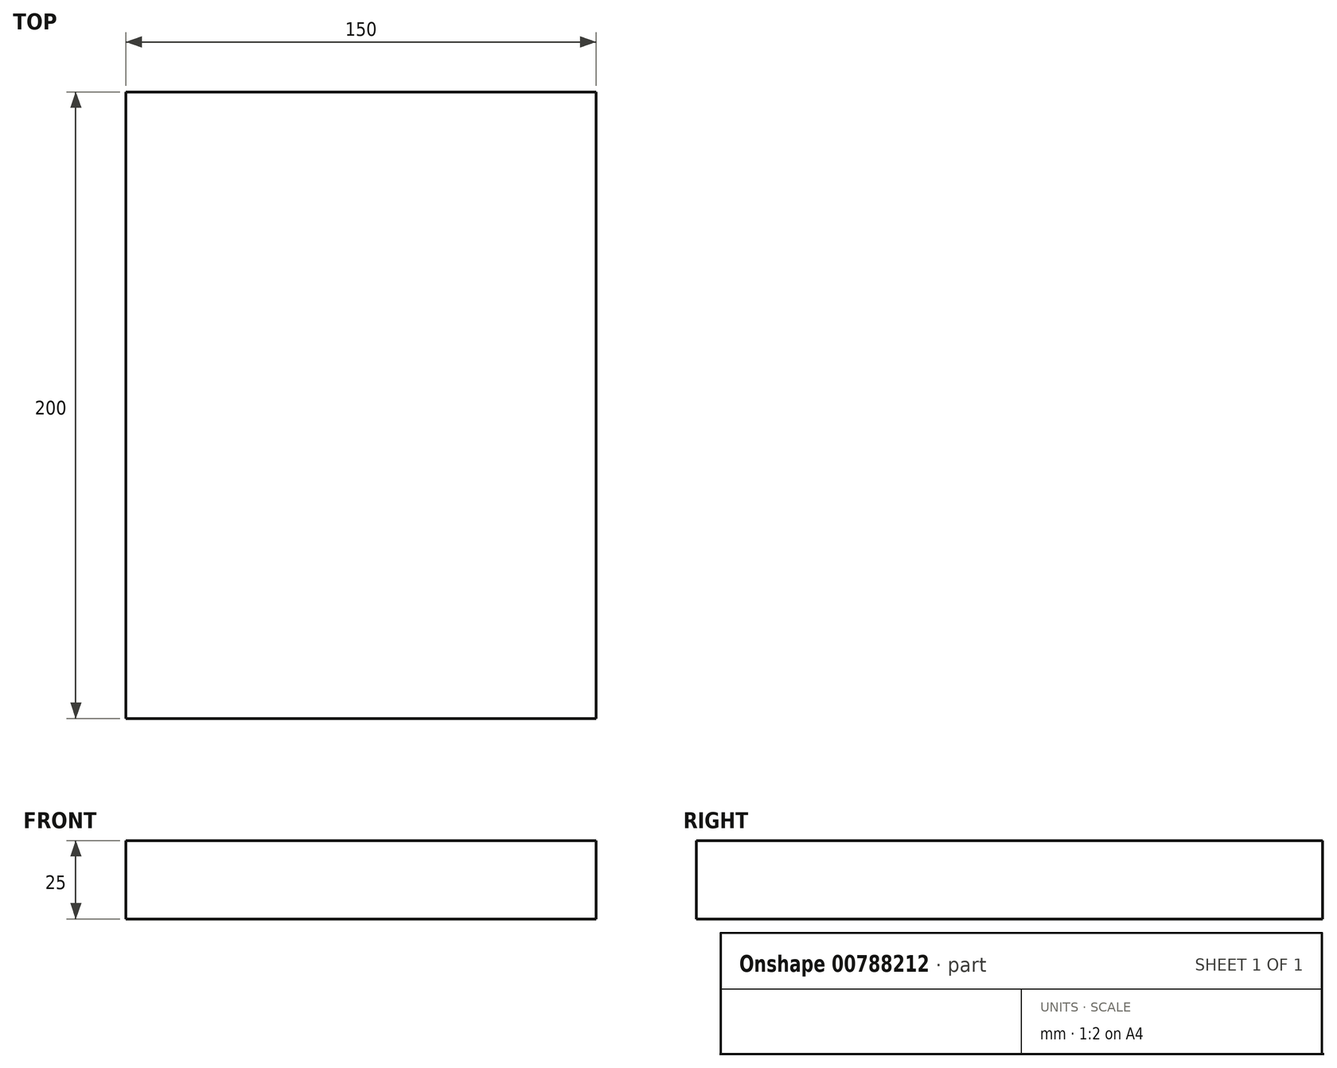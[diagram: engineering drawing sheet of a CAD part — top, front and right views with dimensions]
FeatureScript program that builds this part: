
annotation { "Feature Type Name" : "Feature", "Feature Type Description" : "" }
export const myFeature = defineFeature(function(context is Context, id is Id, definition is map)
    precondition{}
    {
        {
            var Q0;
            Q0=qCreatedBy(makeId("Top.planeOp"),FACE);
            var sketch = newSketch(context, id + "F0", { "sketchPlane" : qUnion([Q0])});
            skLineSegment(sketch, "E0.bottom", {"start": v(-70.79, 113) * mm, "end": v(79.21, 113) * mm});
            skLineSegment(sketch, "E0.top", {"start": v(-70.79, -87) * mm, "end": v(79.21, -87) * mm});
            skLineSegment(sketch, "E0.left", {"start": v(-70.79, 113) * mm, "end": v(-70.79, -87) * mm});
            skLineSegment(sketch, "E0.right", {"start": v(79.21, 113) * mm, "end": v(79.21, -87) * mm});
            skSolve(sketch);
        }
        {
            var Q0;
            Q0 = qSketchRegion(id + "F0", true);
            extrude(context, id + "F1", {"entities" : qUnion([Q0]), "depth" : 25 * mm, "offsetDistance" : 25.4 * mm});
        }
    });
